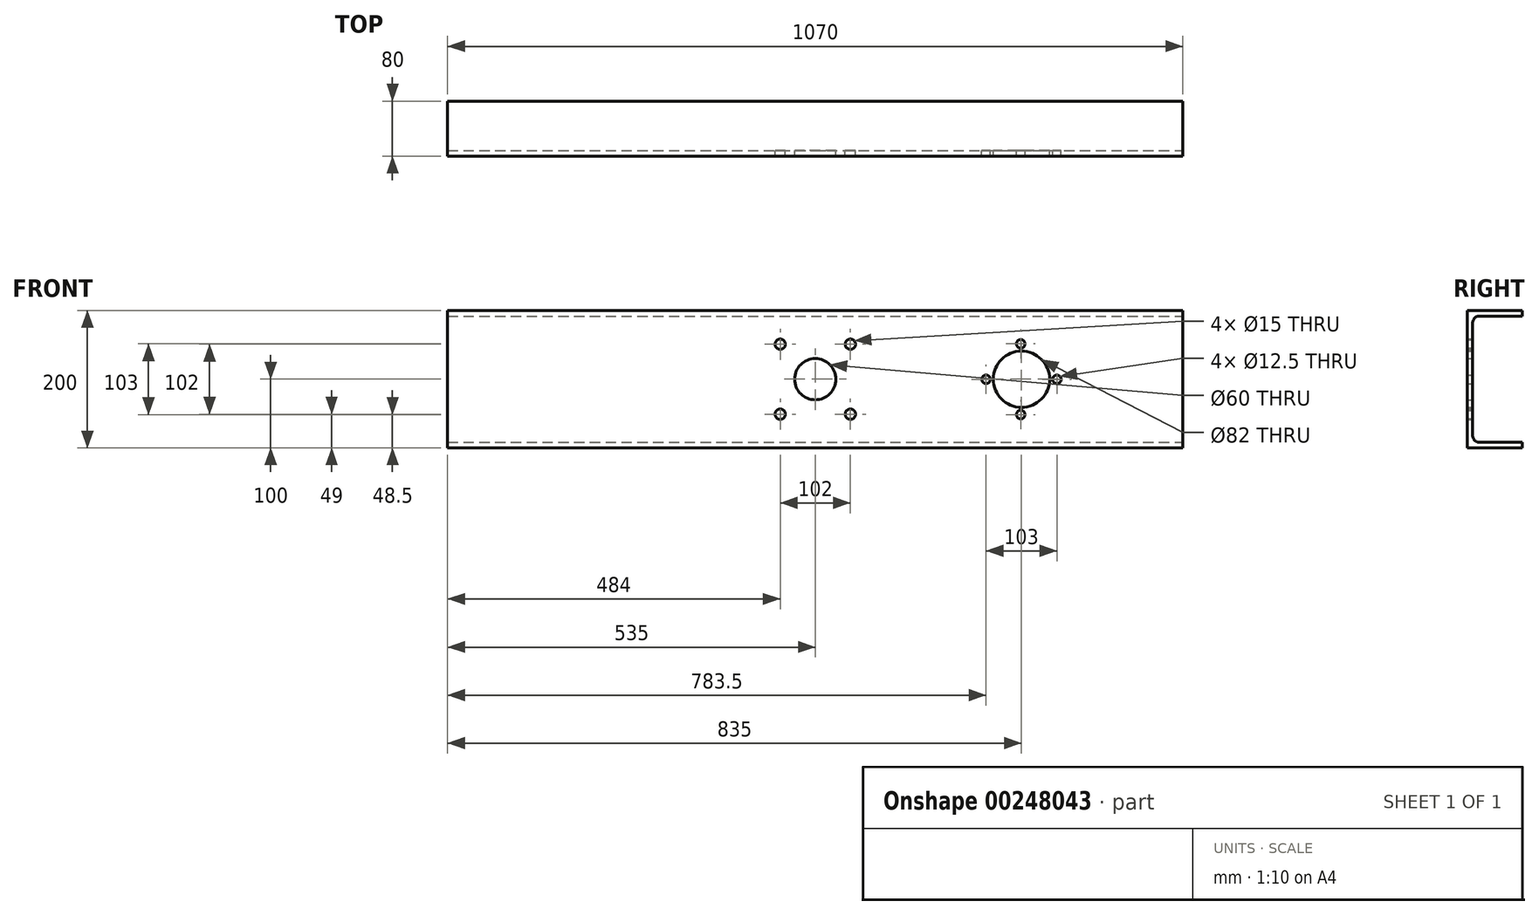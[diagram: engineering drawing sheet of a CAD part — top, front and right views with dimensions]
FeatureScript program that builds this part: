
annotation { "Feature Type Name" : "Feature", "Feature Type Description" : "" }
export const myFeature = defineFeature(function(context is Context, id is Id, definition is map)
    precondition{}
    {
        {
            var Q0;
            Q0=qCreatedBy(makeId("Front.planeOp"),FACE);
            var sketch = newSketch(context, id + "F0", { "sketchPlane" : qUnion([Q0])});
            skLineSegment(sketch, "E0.bottom", {"start": v(-535, 100) * mm, "end": v(535, 100) * mm});
            skLineSegment(sketch, "E0.top", {"start": v(-535, -100) * mm, "end": v(535, -100) * mm});
            skLineSegment(sketch, "E0.left", {"start": v(-535, 100) * mm, "end": v(-535, -100) * mm});
            skLineSegment(sketch, "E0.right", {"start": v(535, 100) * mm, "end": v(535, -100) * mm});
            skPoint(sketch, "E0.middle", {"position": v(0, 0) * mm});
            skPoint(sketch, "E1", {"position": v(-51, 51) * mm});
            skPoint(sketch, "E2", {"position": v(51, 51) * mm});
            skPoint(sketch, "E3", {"position": v(51, -51) * mm});
            skPoint(sketch, "E4", {"position": v(-51, -51) * mm});
            skPoint(sketch, "E5", {"position": v(300, 0) * mm});
            skPoint(sketch, "E6", {"position": v(298.97, 51.5) * mm});
            skPoint(sketch, "E7.1.0", {"position": v(248.5, -0.2) * mm});
            skPoint(sketch, "E7.2.0", {"position": v(298.97, -51.5) * mm});
            skPoint(sketch, "E7.3.0", {"position": v(351.5, -0.2) * mm});
            skSolve(sketch);
        }
        {
            var Q0;
            Q0 = qSketchRegion(id + "F0", true);
            extrude(context, id + "F1", {"entities" : qUnion([Q0]), "depth" : 80 * mm});
        }
        {
            var Q0;
            Q0=makeQuery(id+"F1.opExtrude","CAP_FACE",FACE,{"disambiguationData":[OSD([sQuery(id+"F0.wireOp",EDGE,"E0.bottom"),sQuery(id+"F0.wireOp",EDGE,"E0.top"),sQuery(id+"F0.wireOp",EDGE,"E0.left"),sQuery(id+"F0.wireOp",EDGE,"E0.right")])],"isStart":true});
            var Q1;
            Q1=makeQuery(id+"F1.opExtrude","SWEPT_FACE",FACE,{"disambiguationData":[OSD([sQuery(id+"F0.wireOp",EDGE,"E0.left")])]});
            var Q2;
            Q2=makeQuery(id+"F1.opExtrude","SWEPT_FACE",FACE,{"disambiguationData":[OSD([sQuery(id+"F0.wireOp",EDGE,"E0.right")])]});
            shell(context, id + "F2", {"entities" : qUnion([Q0, Q1, Q2]), "thickness" : 8 * mm});
        }
        {
            var Q0;
            Q0=sQuery(id+"F0.wireOp",VERTEX,"E0.middle");
            var Q1;
            Q1=makeQuery(id+"F1.opExtrude","SWEPT_BODY",BODY,{"disambiguationData":[OSD([sQuery(id+"F0.wireOp",EDGE,"E0.bottom"),sQuery(id+"F0.wireOp",EDGE,"E0.top"),sQuery(id+"F0.wireOp",EDGE,"E0.left"),sQuery(id+"F0.wireOp",EDGE,"E0.right")])]});
            hole(context, id + "F3", {"style" : HoleStyle.SIMPLE, "endStyle" : HoleEndStyle.THROUGH, "oppositeDirection" : true, "holeDiameter" : 60 * mm, "tappedDepth" : 12 * mm, "tapClearance" : 3, "locations" : qUnion([Q0]), "scope" : qUnion([Q1])});
        }
        {
            var Q0;
            {var subQ0=sQuery(id+"F0.wireOp",EDGE,"E0.top");Q0=makeQuery(id+"F2.opShell","OFFSET_EDGE",EDGE,{"disambiguationData":[OSD([subQ0]),TDD([makeQuery(id+"F1.opExtrude","CAP_EDGE",EDGE,{"disambiguationData":[OSD([subQ0])],"isStart":false})])]});}
            var Q1;
            {var subQ0=sQuery(id+"F0.wireOp",EDGE,"E0.bottom");Q1=makeQuery(id+"F2.opShell","OFFSET_EDGE",EDGE,{"disambiguationData":[OSD([subQ0]),TDD([makeQuery(id+"F1.opExtrude","CAP_EDGE",EDGE,{"disambiguationData":[OSD([subQ0])],"isStart":false})])]});}
            fillet(context, id + "F4", {"entities" : qUnion([Q0, Q1]), "radius" : 10 * mm, "tangentPropagation" : true, "allowEdgeOverflow" : false});
        }
        {
            var Q0;
            Q0=sQuery(id+"F0.wireOp",VERTEX,"E1");
            var Q1;
            Q1=sQuery(id+"F0.wireOp",VERTEX,"E2");
            var Q2;
            Q2=sQuery(id+"F0.wireOp",VERTEX,"E3");
            var Q3;
            Q3=sQuery(id+"F0.wireOp",VERTEX,"E4");
            var Q4;
            Q4=makeQuery(id+"F1.opExtrude","SWEPT_BODY",BODY,{"disambiguationData":[OSD([sQuery(id+"F0.wireOp",EDGE,"E0.bottom"),sQuery(id+"F0.wireOp",EDGE,"E0.top"),sQuery(id+"F0.wireOp",EDGE,"E0.left"),sQuery(id+"F0.wireOp",EDGE,"E0.right")])]});
            hole(context, id + "F5", {"style" : HoleStyle.SIMPLE, "endStyle" : HoleEndStyle.THROUGH, "oppositeDirection" : true, "standardTappedOrClearance" : lookupTablePath({ "standard" : "ISO", "size" : "15", "type" : "Drilled" }), "standardBlindInLast" : lookupTablePath({ "standard" : "ISO", "size" : "15", "type" : "Drilled" }), "holeDiameter" : 15 * mm, "tappedDepth" : 12 * mm, "tapClearance" : 3, "locations" : qUnion([Q0, Q1, Q2, Q3]), "scope" : qUnion([Q4])});
        }
        {
            var Q0;
            Q0=sQuery(id+"F0.wireOp",VERTEX,"E5");
            var Q1;
            Q1=makeQuery(id+"F1.opExtrude","SWEPT_BODY",BODY,{"disambiguationData":[OSD([sQuery(id+"F0.wireOp",EDGE,"E0.bottom"),sQuery(id+"F0.wireOp",EDGE,"E0.top"),sQuery(id+"F0.wireOp",EDGE,"E0.left"),sQuery(id+"F0.wireOp",EDGE,"E0.right")])]});
            hole(context, id + "F6", {"style" : HoleStyle.SIMPLE, "endStyle" : HoleEndStyle.THROUGH, "oppositeDirection" : true, "holeDiameter" : 82 * mm, "tappedDepth" : 12 * mm, "tapClearance" : 3, "locations" : qUnion([Q0]), "scope" : qUnion([Q1])});
        }
        {
            var Q0;
            Q0=sQuery(id+"F0.wireOp",VERTEX,"E7.1.0");
            var Q1;
            Q1=sQuery(id+"F0.wireOp",VERTEX,"E6");
            var Q2;
            Q2=sQuery(id+"F0.wireOp",VERTEX,"E7.3.0");
            var Q3;
            Q3=sQuery(id+"F0.wireOp",VERTEX,"E7.2.0");
            var Q4;
            Q4=makeQuery(id+"F1.opExtrude","SWEPT_BODY",BODY,{"disambiguationData":[OSD([sQuery(id+"F0.wireOp",EDGE,"E0.bottom"),sQuery(id+"F0.wireOp",EDGE,"E0.top"),sQuery(id+"F0.wireOp",EDGE,"E0.left"),sQuery(id+"F0.wireOp",EDGE,"E0.right")])]});
            hole(context, id + "F7", {"style" : HoleStyle.SIMPLE, "endStyle" : HoleEndStyle.THROUGH, "oppositeDirection" : true, "holeDiameter" : 12.5 * mm, "tappedDepth" : 12 * mm, "tapClearance" : 3, "locations" : qUnion([Q0, Q1, Q2, Q3]), "scope" : qUnion([Q4])});
        }
    });
